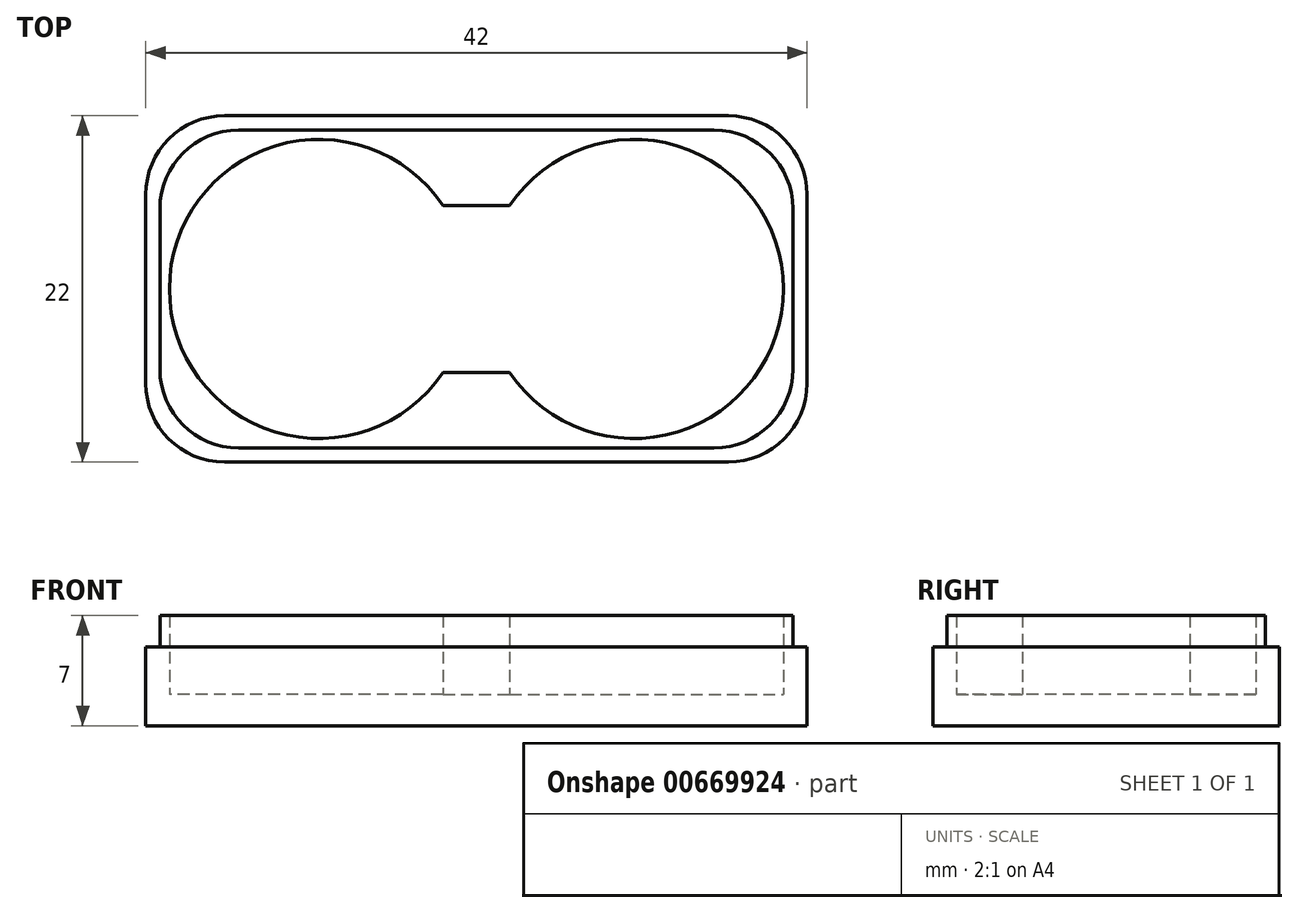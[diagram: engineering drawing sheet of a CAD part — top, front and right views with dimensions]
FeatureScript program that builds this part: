
annotation { "Feature Type Name" : "Feature", "Feature Type Description" : "" }
export const myFeature = defineFeature(function(context is Context, id is Id, definition is map)
    precondition{}
    {
        {
            var Q0;
            Q0=qCreatedBy(makeId("Top.planeOp"),FACE);
            var sketch = newSketch(context, id + "F0", { "sketchPlane" : qUnion([Q0])});
            skLineSegment(sketch, "E0.bottom", {"start": v(-18.88, 16.3) * mm, "end": v(23.12, 16.3) * mm});
            skLineSegment(sketch, "E0.top", {"start": v(-18.88, -5.7) * mm, "end": v(23.12, -5.7) * mm});
            skLineSegment(sketch, "E0.left", {"start": v(-18.88, 16.3) * mm, "end": v(-18.88, -5.7) * mm});
            skLineSegment(sketch, "E0.right", {"start": v(23.12, 16.3) * mm, "end": v(23.12, -5.7) * mm});
            skCircle(sketch, "E1", {"center": v(-7.88, 5.3) * mm, "radius": 9.5 * mm});
            skCircle(sketch, "E2", {"center": v(12.12, 5.3) * mm, "radius": 9.5 * mm});
            skLineSegment(sketch, "E3.bottom", {"start": v(0, 10.61) * mm, "end": v(4.24, 10.61) * mm});
            skLineSegment(sketch, "E3.top", {"start": v(0, 0) * mm, "end": v(4.24, 0) * mm});
            skLineSegment(sketch, "E3.left", {"start": v(0, 10.61) * mm, "end": v(0, 0) * mm});
            skLineSegment(sketch, "E3.right", {"start": v(4.24, 10.61) * mm, "end": v(4.24, 0) * mm});
            skSolve(sketch);
        }
        {
            var Q0;
            Q0 = qSketchRegion(id + "F0", true);
            extrude(context, id + "F1", {"entities" : qUnion([Q0]), "depth" : 5 * mm, "offsetDistance" : 25 * mm});
        }
        {
            var Q0;
            Q0=makeQuery(id+"F1.opExtrude","CAP_FACE",FACE,{"disambiguationData":[OSD([sQuery(id+"F0.wireOp",EDGE,"E0.bottom"),sQuery(id+"F0.wireOp",EDGE,"E0.top"),sQuery(id+"F0.wireOp",EDGE,"E0.left"),sQuery(id+"F0.wireOp",EDGE,"E0.right"),sQuery(id+"F0.wireOp",EDGE,"E1"),sQuery(id+"F0.wireOp",EDGE,"E2"),sQuery(id+"F0.wireOp",EDGE,"E3.bottom"),sQuery(id+"F0.wireOp",EDGE,"E3.top")])],"isStart":true});
            var sketch = newSketch(context, id + "F2", { "sketchPlane" : qUnion([Q0])});
            skLineSegment(sketch, "E4.bottom", {"start": v(-18.88, 5.7) * mm, "end": v(23.12, 5.7) * mm});
            skLineSegment(sketch, "E4.top", {"start": v(-18.88, -16.3) * mm, "end": v(23.12, -16.3) * mm});
            skLineSegment(sketch, "E4.left", {"start": v(-18.88, 5.7) * mm, "end": v(-18.88, -16.3) * mm});
            skLineSegment(sketch, "E4.right", {"start": v(23.12, 5.7) * mm, "end": v(23.12, -16.3) * mm});
            skSolve(sketch);
        }
        {
            var Q0;
            Q0 = qSketchRegion(id + "F2", true);
            extrude(context, id + "F3", {"entities" : qUnion([Q0]), "operationType" : NewBodyOperationType.ADD, "depth" : 2 * mm, "offsetDistance" : 25 * mm});
        }
        {
            var Q0;
            Q0=makeQuery(id+"F1.opExtrude","CAP_FACE",FACE,{"disambiguationData":[OSD([sQuery(id+"F0.wireOp",EDGE,"E0.bottom"),sQuery(id+"F0.wireOp",EDGE,"E0.top"),sQuery(id+"F0.wireOp",EDGE,"E0.left"),sQuery(id+"F0.wireOp",EDGE,"E0.right"),sQuery(id+"F0.wireOp",EDGE,"E1"),sQuery(id+"F0.wireOp",EDGE,"E2"),sQuery(id+"F0.wireOp",EDGE,"E3.bottom"),sQuery(id+"F0.wireOp",EDGE,"E3.top")])],"isStart":false});
            var sketch = newSketch(context, id + "F4", { "sketchPlane" : qUnion([Q0])});
            skLineSegment(sketch, "E5.bottom", {"start": v(-17.98, 15.4) * mm, "end": v(22.22, 15.4) * mm});
            skLineSegment(sketch, "E5.top", {"start": v(-17.98, -4.8) * mm, "end": v(22.22, -4.8) * mm});
            skLineSegment(sketch, "E5.left", {"start": v(-17.98, 15.4) * mm, "end": v(-17.98, -4.8) * mm});
            skLineSegment(sketch, "E5.right", {"start": v(22.22, 15.4) * mm, "end": v(22.22, -4.8) * mm});
            skLineSegment(sketch, "E6.bottom", {"start": v(-18.88, 16.3) * mm, "end": v(23.12, 16.3) * mm});
            skLineSegment(sketch, "E6.top", {"start": v(-18.88, -5.7) * mm, "end": v(23.12, -5.7) * mm});
            skLineSegment(sketch, "E6.left", {"start": v(-18.88, 16.3) * mm, "end": v(-18.88, -5.7) * mm});
            skLineSegment(sketch, "E6.right", {"start": v(23.12, 16.3) * mm, "end": v(23.12, -5.7) * mm});
            skSolve(sketch);
        }
        {
            var Q0;
            Q0 = qSketchRegion(id + "F4", true);
            extrude(context, id + "F5", {"entities" : qUnion([Q0]), "operationType" : NewBodyOperationType.REMOVE, "oppositeDirection" : true, "depth" : 2 * mm, "offsetDistance" : 25 * mm});
        }
        {
            var Q0;
            Q0=makeQuery(id+"F3.boolean.opBoolean","MERGE",EDGE,{"derivedFrom":[makeQuery(id+"F1.opExtrude","SWEPT_EDGE",EDGE,{"disambiguationData":[OSD([sQuery(id+"F0.wireOp",EDGE,"E0.bottom"),sQuery(id+"F0.wireOp",EDGE,"E0.left")])]}),makeQuery(id+"F3.opExtrude","SWEPT_EDGE",EDGE,{"disambiguationData":[OSD([sQuery(id+"F2.wireOp",EDGE,"E4.top"),sQuery(id+"F2.wireOp",EDGE,"E4.left")])]})]});
            var Q1;
            Q1=makeQuery(id+"F3.boolean.opBoolean","MERGE",EDGE,{"derivedFrom":[makeQuery(id+"F1.opExtrude","SWEPT_EDGE",EDGE,{"disambiguationData":[OSD([sQuery(id+"F0.wireOp",EDGE,"E0.top"),sQuery(id+"F0.wireOp",EDGE,"E0.left")])]}),makeQuery(id+"F3.opExtrude","SWEPT_EDGE",EDGE,{"disambiguationData":[OSD([sQuery(id+"F2.wireOp",EDGE,"E4.bottom"),sQuery(id+"F2.wireOp",EDGE,"E4.left")])]})]});
            var Q2;
            Q2=makeQuery(id+"F3.boolean.opBoolean","MERGE",EDGE,{"derivedFrom":[makeQuery(id+"F1.opExtrude","SWEPT_EDGE",EDGE,{"disambiguationData":[OSD([sQuery(id+"F0.wireOp",EDGE,"E0.top"),sQuery(id+"F0.wireOp",EDGE,"E0.right")])]}),makeQuery(id+"F3.opExtrude","SWEPT_EDGE",EDGE,{"disambiguationData":[OSD([sQuery(id+"F2.wireOp",EDGE,"E4.bottom"),sQuery(id+"F2.wireOp",EDGE,"E4.right")])]})]});
            var Q3;
            Q3=makeQuery(id+"F3.boolean.opBoolean","MERGE",EDGE,{"derivedFrom":[makeQuery(id+"F1.opExtrude","SWEPT_EDGE",EDGE,{"disambiguationData":[OSD([sQuery(id+"F0.wireOp",EDGE,"E0.bottom"),sQuery(id+"F0.wireOp",EDGE,"E0.right")])]}),makeQuery(id+"F3.opExtrude","SWEPT_EDGE",EDGE,{"disambiguationData":[OSD([sQuery(id+"F2.wireOp",EDGE,"E4.top"),sQuery(id+"F2.wireOp",EDGE,"E4.right")])]})]});
            var Q4;
            Q4=makeQuery(id+"F5.boolean.opBoolean","COPY",EDGE,{"derivedFrom":makeQuery(id+"F5.opExtrude","SWEPT_EDGE",EDGE,{"disambiguationData":[OSD([sQuery(id+"F4.wireOp",EDGE,"E5.bottom"),sQuery(id+"F4.wireOp",EDGE,"E5.right")])]})});
            var Q5;
            Q5=makeQuery(id+"F5.boolean.opBoolean","COPY",EDGE,{"derivedFrom":makeQuery(id+"F5.opExtrude","SWEPT_EDGE",EDGE,{"disambiguationData":[OSD([sQuery(id+"F4.wireOp",EDGE,"E5.top"),sQuery(id+"F4.wireOp",EDGE,"E5.left")])]})});
            var Q6;
            Q6=makeQuery(id+"F5.boolean.opBoolean","COPY",EDGE,{"derivedFrom":makeQuery(id+"F5.opExtrude","SWEPT_EDGE",EDGE,{"disambiguationData":[OSD([sQuery(id+"F4.wireOp",EDGE,"E5.top"),sQuery(id+"F4.wireOp",EDGE,"E5.right")])]})});
            var Q7;
            Q7=makeQuery(id+"F5.boolean.opBoolean","COPY",EDGE,{"derivedFrom":makeQuery(id+"F5.opExtrude","SWEPT_EDGE",EDGE,{"disambiguationData":[OSD([sQuery(id+"F4.wireOp",EDGE,"E5.bottom"),sQuery(id+"F4.wireOp",EDGE,"E5.left")])]})});
            fillet(context, id + "F6", {"entities" : qUnion([Q0, Q1, Q2, Q3, Q4, Q5, Q6, Q7]), "radius" : 5 * mm, "tangentPropagation" : true, "allowEdgeOverflow" : false});
        }
    });
